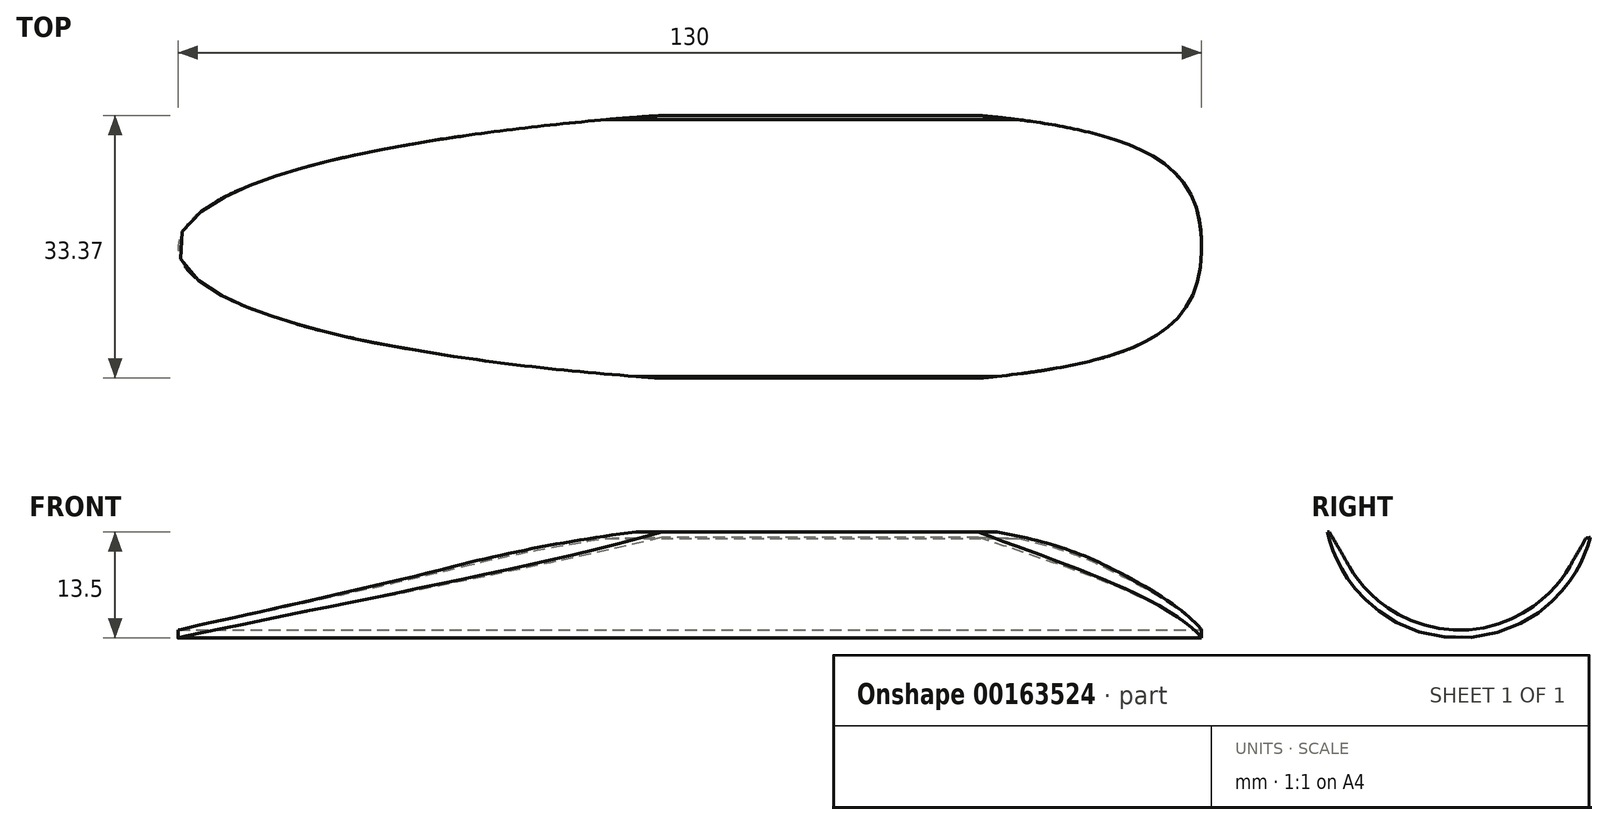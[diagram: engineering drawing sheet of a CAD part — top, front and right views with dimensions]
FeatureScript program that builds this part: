
annotation { "Feature Type Name" : "Feature", "Feature Type Description" : "" }
export const myFeature = defineFeature(function(context is Context, id is Id, definition is map)
    precondition{}
    {
        {
            var Q0;
            Q0=qCreatedBy(makeId("Top.planeOp"),FACE);
            var sketch = newSketch(context, id + "F0", { "sketchPlane" : qUnion([Q0])});
            skLineSegment(sketch, "E0", {"start": v(-65, 0) * mm, "end": v(65, 0) * mm, "construction": true});
            skLineSegment(sketch, "E1", {"start": v(56.95, 12.5) * mm, "end": v(56.95, -12.5) * mm, "construction": true});
            skLineSegment(sketch, "E2", {"start": v(-45.43, 11) * mm, "end": v(-45.43, -11) * mm, "construction": true});
            skFitSpline(sketch, "E3", {"points": [v(-65, 0) * mm, v(-45.43, 11) * mm, v(56.95, 12.5) * mm, v(65, 0) * mm, v(56.95, -12.5) * mm, v(-45.43, -11) * mm, v(-65, 0) * mm]});
            skSolve(sketch);
        }
        {
            var Q0;
            Q0=makeQuery(id+"F0.imprint","IMPRINT",FACE,{"disambiguationData":[TD([[makeQuery(id+"F0.imprint","IMPRINT",EDGE,{"derivedFrom":sQuery(id+"F0.wireOp",EDGE,"E3")}),-1.0]])]});
            extrude(context, id + "F1", {"entities" : qUnion([Q0]), "endBound" : BoundingType.SYMMETRIC, "oppositeDirection" : true, "depth" : 20 * mm});
        }
        {
            var Q0;
            Q0=qCreatedBy(makeId("Right.planeOp"),FACE);
            var sketch = newSketch(context, id + "F2", { "sketchPlane" : qUnion([Q0])});
            skArc(sketch, "E4", {"start": v(-13.91, 0) * mm, "mid": v(0.09, -8.08) * mm, "end": v(14.09, 0) * mm});
            skLineSegment(sketch, "E5", {"start": v(14.09, 0) * mm, "end": v(16.16, 3.6) * mm});
            skLineSegment(sketch, "E6", {"start": v(-13.91, 0) * mm, "end": v(-16.46, 4.4) * mm});
            skLineSegment(sketch, "E7", {"start": v(16.16, 3.6) * mm, "end": v(19.04, 4.1) * mm});
            skLineSegment(sketch, "E8", {"start": v(19.04, 4.1) * mm, "end": v(19.04, 11) * mm});
            skLineSegment(sketch, "E9", {"start": v(19.04, 11) * mm, "end": v(-19.27, 11) * mm});
            skLineSegment(sketch, "E10", {"start": v(-19.27, 11) * mm, "end": v(-19.27, 4.59) * mm});
            skLineSegment(sketch, "E11", {"start": v(-19.27, 4.59) * mm, "end": v(-16.46, 4.4) * mm});
            skSolve(sketch);
        }
        {
            var Q0;
            Q0=qSketchRegion(id+"F2",true);
            extrude(context, id + "F3", {"entities" : qUnion([Q0]), "operationType" : NewBodyOperationType.REMOVE, "endBound" : BoundingType.SYMMETRIC, "oppositeDirection" : true, "depth" : 200 * mm});
        }
        {
            var Q0;
            Q0=qCreatedBy(makeId("Right.planeOp"),FACE);
            var sketch = newSketch(context, id + "F4", { "sketchPlane" : qUnion([Q0])});
            skArc(sketch, "E12.0", {"start": v(-17.06, 7.11) * mm, "mid": v(-0.5, -9.07) * mm, "end": v(17.13, 5.96) * mm});
            skLineSegment(sketch, "E13", {"start": v(-17.06, 7.11) * mm, "end": v(-23.9, -11.4) * mm});
            skLineSegment(sketch, "E14", {"start": v(-23.9, -11.4) * mm, "end": v(20.42, -11.4) * mm});
            skLineSegment(sketch, "E15", {"start": v(20.42, -11.4) * mm, "end": v(17.13, 5.96) * mm});
            skSolve(sketch);
        }
        {
            var Q0;
            Q0 = qSketchRegion(id + "F4", true);
            extrude(context, id + "F5", {"entities" : qUnion([Q0]), "operationType" : NewBodyOperationType.REMOVE, "endBound" : BoundingType.SYMMETRIC, "depth" : 200 * mm});
        }
    });
